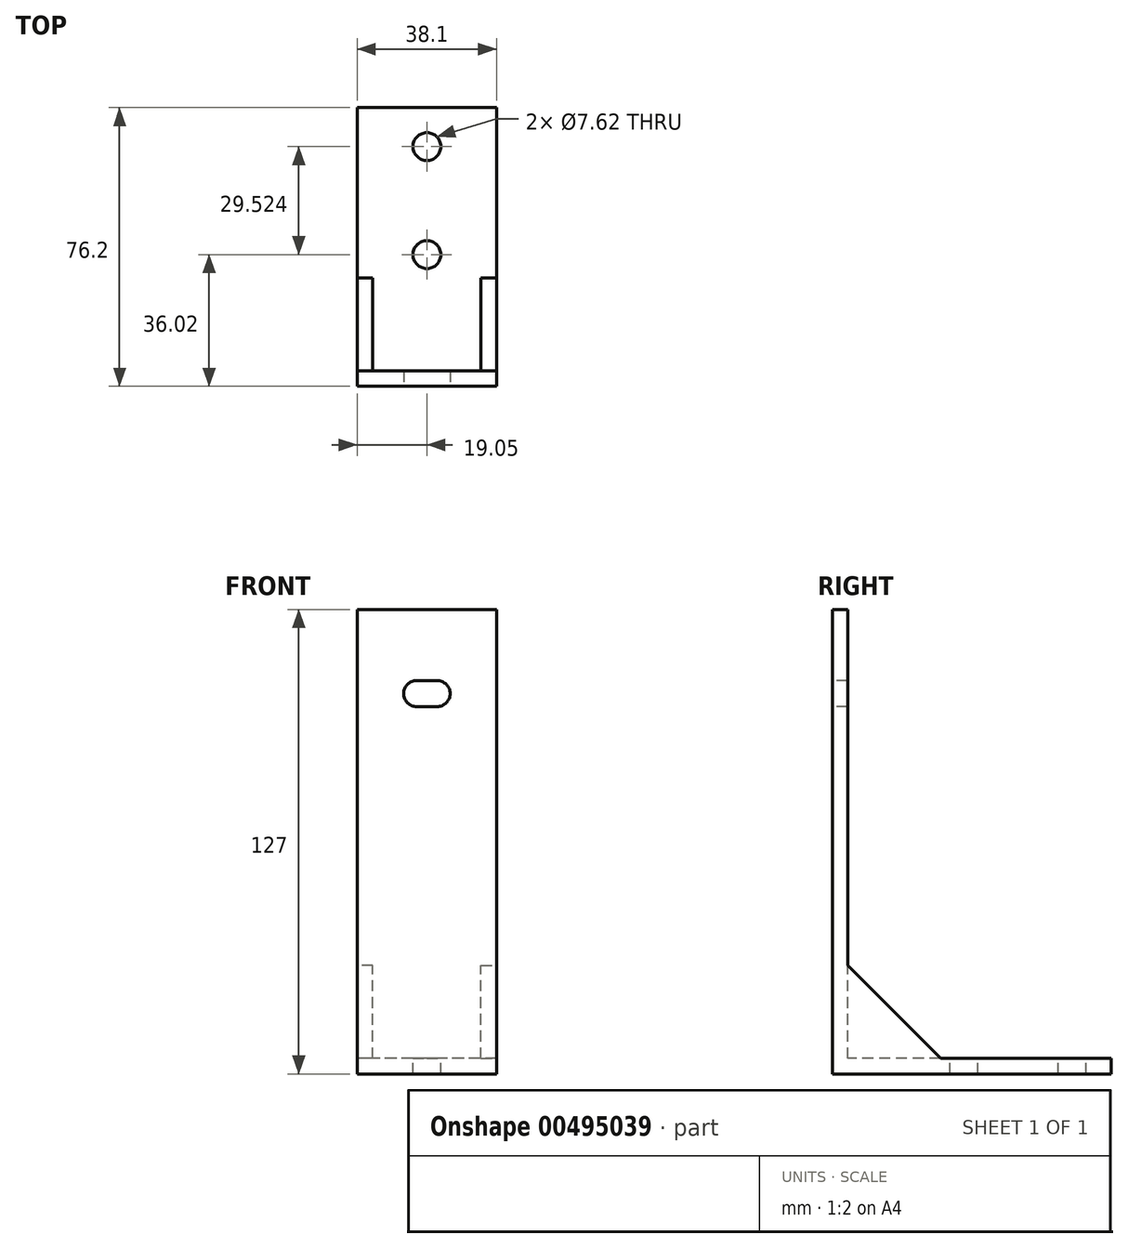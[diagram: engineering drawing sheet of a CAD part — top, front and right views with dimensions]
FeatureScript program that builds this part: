
annotation { "Feature Type Name" : "Feature", "Feature Type Description" : "" }
export const myFeature = defineFeature(function(context is Context, id is Id, definition is map)
    precondition{}
    {
        {
            var Q0;
            Q0=qCreatedBy(makeId("Right.planeOp"),FACE);
            var sketch = newSketch(context, id + "F0", { "sketchPlane" : qUnion([Q0])});
            skLineSegment(sketch, "E0", {"start": v(-36.02, 80.86) * mm, "end": v(-36.02, -46.14) * mm});
            skLineSegment(sketch, "E1", {"start": v(-36.02, -46.14) * mm, "end": v(40.18, -46.14) * mm});
            skLineSegment(sketch, "E2", {"start": v(40.18, -46.14) * mm, "end": v(40.18, -41.9) * mm});
            skLineSegment(sketch, "E3", {"start": v(40.18, -41.9) * mm, "end": v(-31.79, -41.9) * mm});
            skLineSegment(sketch, "E4", {"start": v(-31.79, -41.9) * mm, "end": v(-31.79, 80.86) * mm});
            skLineSegment(sketch, "E5", {"start": v(-31.79, 80.86) * mm, "end": v(-36.02, 80.86) * mm});
            skSolve(sketch);
        }
        {
            var Q0;
            Q0=makeQuery(id+"F0.imprint","IMPRINT",FACE,{"disambiguationData":[TD([[makeQuery(id+"F0.imprint","IMPRINT",EDGE,{"derivedFrom":sQuery(id+"F0.wireOp",EDGE,"E0")}),1.0]])]});
            extrude(context, id + "F1", {"entities" : qUnion([Q0]), "depth" : 38.1 * mm});
        }
        {
            var Q0;
            Q0=makeQuery(id+"F1.opExtrude","SWEPT_FACE",FACE,{"disambiguationData":[OSD([sQuery(id+"F0.wireOp",EDGE,"E0")])]});
            var sketch = newSketch(context, id + "F2", { "sketchPlane" : qUnion([Q0])});
            skLineSegment(sketch, "E6", {"start": v(19.05, 80.86) * mm, "end": v(19.05, -46.14) * mm, "construction": true});
            skLineSegment(sketch, "E7.bottom", {"start": v(16.26, 61.4) * mm, "end": v(21.84, 61.4) * mm});
            skLineSegment(sketch, "E7.top", {"start": v(16.26, 54.3) * mm, "end": v(21.84, 54.3) * mm});
            skLineSegment(sketch, "E7.left", {"start": v(12.7, 57.85) * mm, "end": v(12.7, 57.85) * mm});
            skLineSegment(sketch, "E7.right", {"start": v(25.4, 57.85) * mm, "end": v(25.4, 57.85) * mm});
            skPoint(sketch, "E7.middle", {"position": v(19.05, 57.85) * mm});
            skPoint(sketch, "E8.visualSharp", {"position": v(12.7, 61.4) * mm});
            skArc(sketch, "E8.filletArc", {"start": v(16.26, 61.4) * mm, "mid": v(13.74, 60.37) * mm, "end": v(12.7, 57.85) * mm});
            skPoint(sketch, "E9.visualSharp", {"position": v(25.4, 61.4) * mm});
            skArc(sketch, "E9.filletArc", {"start": v(25.4, 57.85) * mm, "mid": v(24.36, 60.37) * mm, "end": v(21.84, 61.4) * mm});
            skPoint(sketch, "E10.visualSharp", {"position": v(25.4, 54.3) * mm});
            skArc(sketch, "E10.filletArc", {"start": v(21.84, 54.3) * mm, "mid": v(24.36, 55.34) * mm, "end": v(25.4, 57.85) * mm});
            skPoint(sketch, "E11.visualSharp", {"position": v(12.7, 54.3) * mm});
            skArc(sketch, "E11.filletArc", {"start": v(12.7, 57.85) * mm, "mid": v(13.74, 55.34) * mm, "end": v(16.26, 54.3) * mm});
            skSolve(sketch);
        }
        {
            var Q0;
            Q0=makeQuery(id+"F2.imprint","IMPRINT",FACE,{"disambiguationData":[TD([[makeQuery(id+"F2.imprint","IMPRINT",EDGE,{"derivedFrom":sQuery(id+"F2.wireOp",EDGE,"E7.bottom")}),-1.0]])]});
            extrude(context, id + "F3", {"entities" : qUnion([Q0]), "operationType" : NewBodyOperationType.REMOVE, "oppositeDirection" : true, "depth" : 25.4 * mm});
        }
        {
            var Q0;
            Q0=makeQuery(id+"F1.opExtrude","CAP_FACE",FACE,{"disambiguationData":[OSD([sQuery(id+"F0.wireOp",EDGE,"E0"),sQuery(id+"F0.wireOp",EDGE,"E1"),sQuery(id+"F0.wireOp",EDGE,"E2"),sQuery(id+"F0.wireOp",EDGE,"E3"),sQuery(id+"F0.wireOp",EDGE,"E4"),sQuery(id+"F0.wireOp",EDGE,"E5")])],"isStart":false});
            var sketch = newSketch(context, id + "F4", { "sketchPlane" : qUnion([Q0])});
            skLineSegment(sketch, "E12", {"start": v(-6.39, -41.9) * mm, "end": v(-31.79, -41.9) * mm});
            skLineSegment(sketch, "E13", {"start": v(-31.79, -41.9) * mm, "end": v(-31.79, -16.5) * mm});
            skLineSegment(sketch, "E14", {"start": v(-31.79, -16.5) * mm, "end": v(-6.39, -41.9) * mm});
            skSolve(sketch);
        }
        {
            var Q0;
            Q0 = qSketchRegion(id + "F4", true);
            extrude(context, id + "F5", {"entities" : qUnion([Q0]), "operationType" : NewBodyOperationType.ADD, "oppositeDirection" : true, "depth" : 4.23 * mm});
        }
        {
            var Q0;
            Q0=makeQuery(id+"F1.opExtrude","CAP_FACE",FACE,{"disambiguationData":[OSD([sQuery(id+"F0.wireOp",EDGE,"E0"),sQuery(id+"F0.wireOp",EDGE,"E1"),sQuery(id+"F0.wireOp",EDGE,"E2"),sQuery(id+"F0.wireOp",EDGE,"E3"),sQuery(id+"F0.wireOp",EDGE,"E4"),sQuery(id+"F0.wireOp",EDGE,"E5")])],"isStart":true});
            var sketch = newSketch(context, id + "F6", { "sketchPlane" : qUnion([Q0])});
            skLineSegment(sketch, "E15", {"start": v(31.79, -16.5) * mm, "end": v(31.79, -41.9) * mm});
            skLineSegment(sketch, "E16", {"start": v(31.79, -41.9) * mm, "end": v(6.39, -41.9) * mm});
            skLineSegment(sketch, "E17", {"start": v(6.39, -41.9) * mm, "end": v(31.79, -16.5) * mm});
            skSolve(sketch);
        }
        {
            var Q0;
            Q0=makeQuery(id+"F6.imprint","IMPRINT",FACE,{"disambiguationData":[TD([[makeQuery(id+"F6.imprint","IMPRINT",EDGE,{"derivedFrom":sQuery(id+"F6.wireOp",EDGE,"E15")}),1.0]])]});
            extrude(context, id + "F7", {"entities" : qUnion([Q0]), "operationType" : NewBodyOperationType.ADD, "oppositeDirection" : true, "depth" : 4.23 * mm});
        }
        {
            var Q0;
            Q0=makeQuery(id+"F1.opExtrude","SWEPT_FACE",FACE,{"disambiguationData":[OSD([sQuery(id+"F0.wireOp",EDGE,"E3")])]});
            var sketch = newSketch(context, id + "F8", { "sketchPlane" : qUnion([Q0])});
            skLineSegment(sketch, "E18", {"start": v(19.05, -31.79) * mm, "end": v(19.05, 40.18) * mm, "construction": true});
            skPoint(sketch, "E19", {"position": v(19.05, 0) * mm});
            skPoint(sketch, "E20", {"position": v(19.05, 29.52) * mm});
            skSolve(sketch);
        }
        {
            var Q0;
            Q0=sQuery(id+"F8.wireOp",VERTEX,"E19");
            var Q1;
            Q1=sQuery(id+"F8.wireOp",VERTEX,"E20");
            var Q2;
            Q2=makeQuery(id+"F1.opExtrude","SWEPT_BODY",BODY,{"disambiguationData":[OSD([sQuery(id+"F0.wireOp",EDGE,"E0"),sQuery(id+"F0.wireOp",EDGE,"E1"),sQuery(id+"F0.wireOp",EDGE,"E2"),sQuery(id+"F0.wireOp",EDGE,"E3"),sQuery(id+"F0.wireOp",EDGE,"E4"),sQuery(id+"F0.wireOp",EDGE,"E5")])]});
            hole(context, id + "F9", {"style" : HoleStyle.SIMPLE, "endStyle" : HoleEndStyle.BLIND, "holeDiameter" : 7.62 * mm, "holeDepth" : 12.7 * mm, "isTappedThrough" : true, "tappedDepth" : 12.7 * mm, "tapClearance" : 3, "locations" : qUnion([Q0, Q1]), "scope" : qUnion([Q2])});
        }
    });
